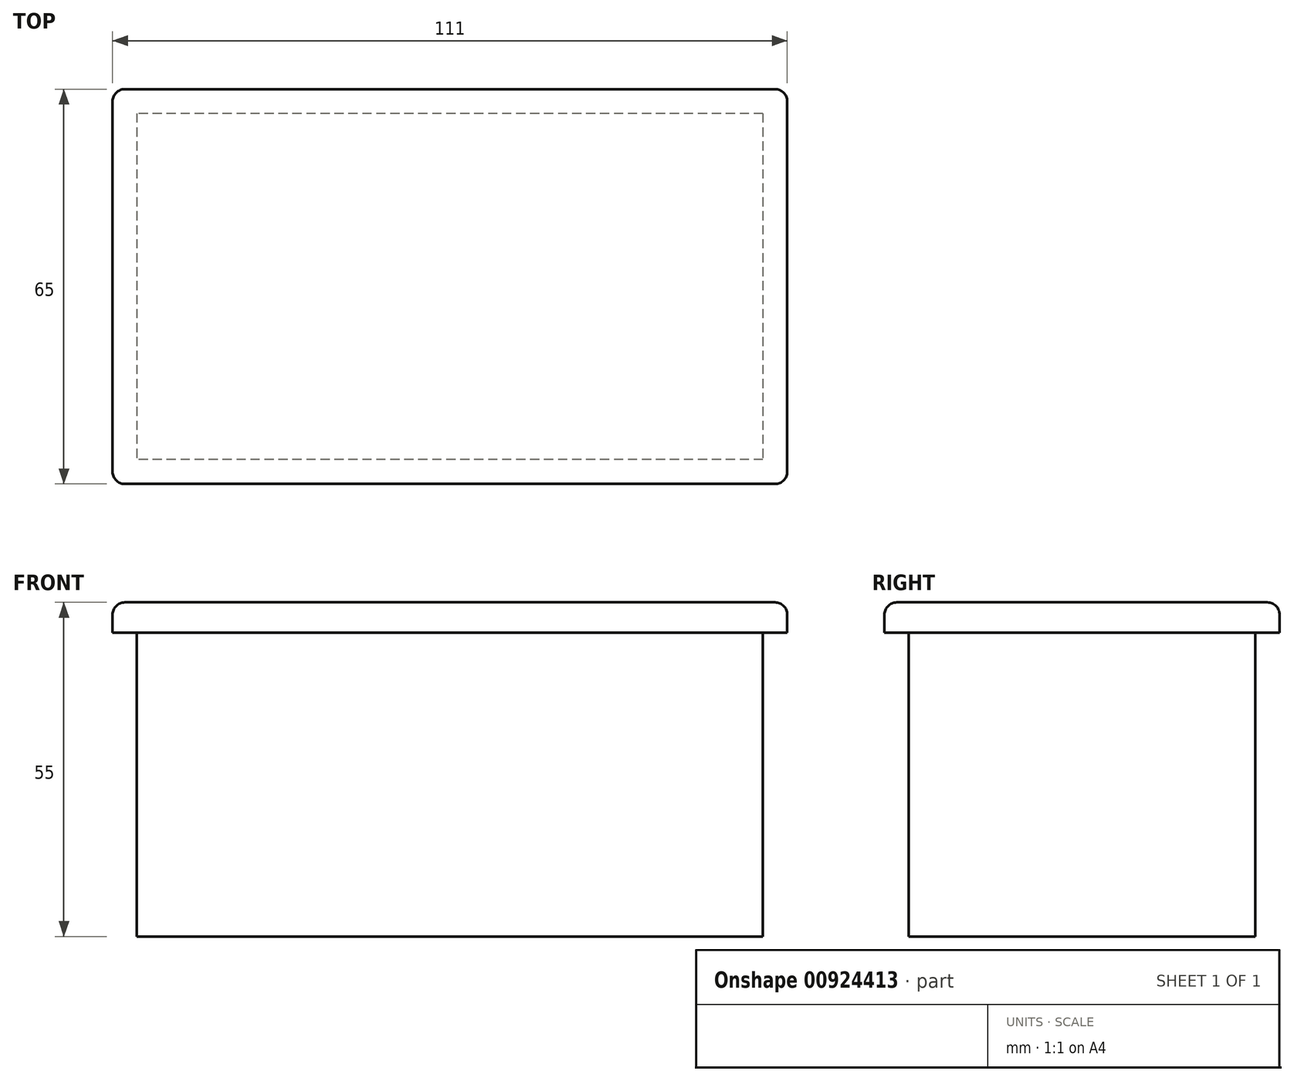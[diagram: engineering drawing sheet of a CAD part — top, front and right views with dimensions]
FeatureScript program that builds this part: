
annotation { "Feature Type Name" : "Feature", "Feature Type Description" : "" }
export const myFeature = defineFeature(function(context is Context, id is Id, definition is map)
    precondition{}
    {
        {
            var Q0;
            Q0=qCreatedBy(makeId("Top.planeOp"),FACE);
            var sketch = newSketch(context, id + "F0", { "sketchPlane" : qUnion([Q0])});
            skLineSegment(sketch, "E0.bottom", {"start": v(55.5, -32.5) * mm, "end": v(-55.5, -32.5) * mm});
            skLineSegment(sketch, "E0.top", {"start": v(55.5, 32.5) * mm, "end": v(-55.5, 32.5) * mm});
            skLineSegment(sketch, "E0.left", {"start": v(55.5, -32.5) * mm, "end": v(55.5, 32.5) * mm});
            skLineSegment(sketch, "E0.right", {"start": v(-55.5, -32.5) * mm, "end": v(-55.5, 32.5) * mm});
            skPoint(sketch, "E0.middle", {"position": v(0, 0) * mm});
            skSolve(sketch);
        }
        {
            var Q0;
            Q0=qSketchRegion(id+"F0",true);
            extrude(context, id + "F1", {"entities" : qUnion([Q0]), "depth" : 5 * mm, "offsetDistance" : 25 * mm});
        }
        {
            var Q0;
            Q0=qCreatedBy(makeId("Top.planeOp"),FACE);
            var sketch = newSketch(context, id + "F2", { "sketchPlane" : qUnion([Q0])});
            skLineSegment(sketch, "E1.bottom", {"start": v(51.5, 28.5) * mm, "end": v(-51.5, 28.5) * mm});
            skLineSegment(sketch, "E1.top", {"start": v(51.5, -28.5) * mm, "end": v(-51.5, -28.5) * mm});
            skLineSegment(sketch, "E1.left", {"start": v(51.5, 28.5) * mm, "end": v(51.5, -28.5) * mm});
            skLineSegment(sketch, "E1.right", {"start": v(-51.5, 28.5) * mm, "end": v(-51.5, -28.5) * mm});
            skPoint(sketch, "E1.middle", {"position": v(0, 0) * mm});
            skSolve(sketch);
        }
        {
            var Q0;
            Q0=qSketchRegion(id+"F2",true);
            extrude(context, id + "F3", {"entities" : qUnion([Q0]), "operationType" : NewBodyOperationType.ADD, "oppositeDirection" : true, "depth" : 50 * mm, "offsetDistance" : 25 * mm});
        }
        {
            var Q0;
            Q0=makeQuery(id+"F1.opExtrude","CAP_FACE",FACE,{"disambiguationData":[OSD([sQuery(id+"F0.wireOp",EDGE,"E0.bottom"),sQuery(id+"F0.wireOp",EDGE,"E0.top"),sQuery(id+"F0.wireOp",EDGE,"E0.left"),sQuery(id+"F0.wireOp",EDGE,"E0.right")])],"isStart":false});
            var Q1;
            Q1=makeQuery(id+"F1.opExtrude","SWEPT_EDGE",EDGE,{"disambiguationData":[OSD([sQuery(id+"F0.wireOp",EDGE,"E0.top"),sQuery(id+"F0.wireOp",EDGE,"E0.right")])]});
            var Q2;
            Q2=makeQuery(id+"F1.opExtrude","SWEPT_EDGE",EDGE,{"disambiguationData":[OSD([sQuery(id+"F0.wireOp",EDGE,"E0.top"),sQuery(id+"F0.wireOp",EDGE,"E0.left")])]});
            var Q3;
            Q3=makeQuery(id+"F1.opExtrude","SWEPT_EDGE",EDGE,{"disambiguationData":[OSD([sQuery(id+"F0.wireOp",EDGE,"E0.bottom"),sQuery(id+"F0.wireOp",EDGE,"E0.left")])]});
            var Q4;
            Q4=makeQuery(id+"F1.opExtrude","SWEPT_EDGE",EDGE,{"disambiguationData":[OSD([sQuery(id+"F0.wireOp",EDGE,"E0.bottom"),sQuery(id+"F0.wireOp",EDGE,"E0.right")])]});
            fillet(context, id + "F4", {"entities" : qUnion([Q0, Q1, Q2, Q3, Q4]), "radius" : 2 * mm, "tangentPropagation" : true, "allowEdgeOverflow" : false});
        }
    });
